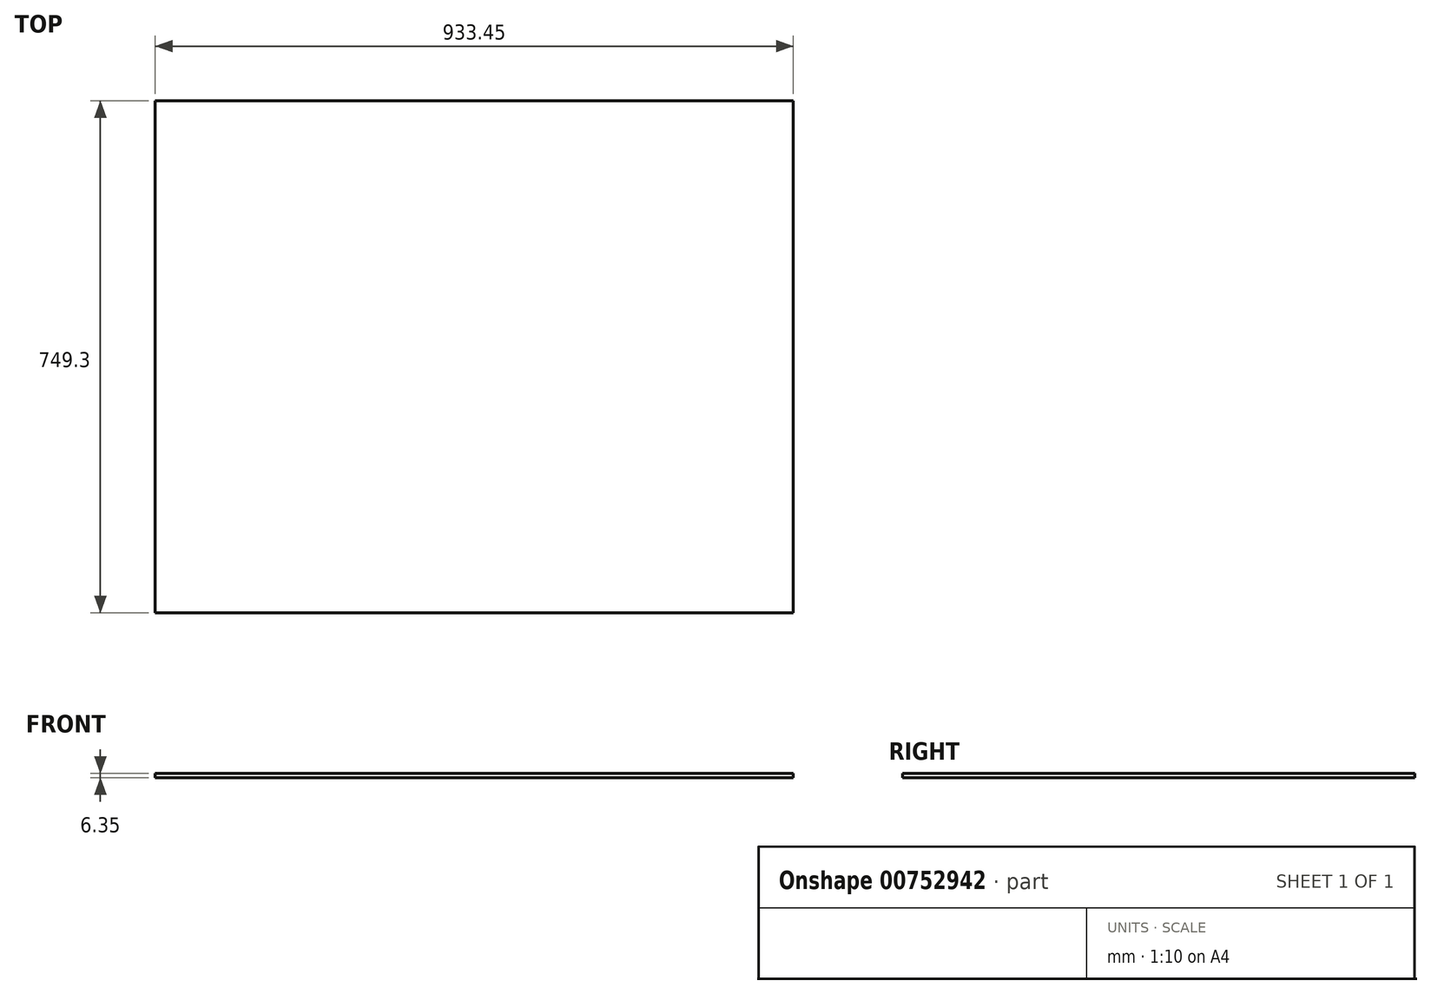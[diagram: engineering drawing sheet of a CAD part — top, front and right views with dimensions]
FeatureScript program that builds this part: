
annotation { "Feature Type Name" : "Feature", "Feature Type Description" : "" }
export const myFeature = defineFeature(function(context is Context, id is Id, definition is map)
    precondition{}
    {
        {
            var Q0;
            Q0=qCreatedBy(makeId("Front.planeOp"),FACE);
            var sketch = newSketch(context, id + "F0", { "sketchPlane" : qUnion([Q0])});
            skLineSegment(sketch, "E0.bottom", {"start": v(0, 0) * mm, "end": v(933.45, 0) * mm});
            skLineSegment(sketch, "E0.top", {"start": v(0, 6.35) * mm, "end": v(933.45, 6.35) * mm});
            skLineSegment(sketch, "E0.left", {"start": v(0, 0) * mm, "end": v(0, 6.35) * mm});
            skLineSegment(sketch, "E0.right", {"start": v(933.45, 0) * mm, "end": v(933.45, 6.35) * mm});
            skSolve(sketch);
        }
        {
            var Q0;
            Q0=makeQuery(id+"F0.imprint","IMPRINT",FACE,{"disambiguationData":[TD([[makeQuery(id+"F0.imprint","IMPRINT",EDGE,{"derivedFrom":sQuery(id+"F0.wireOp",EDGE,"E0.bottom")}),1.0]])]});
            extrude(context, id + "F1", {"entities" : qUnion([Q0]), "depth" : 749.3 * mm, "offsetDistance" : 25.4 * mm, "symmetric" : true});
        }
    });
